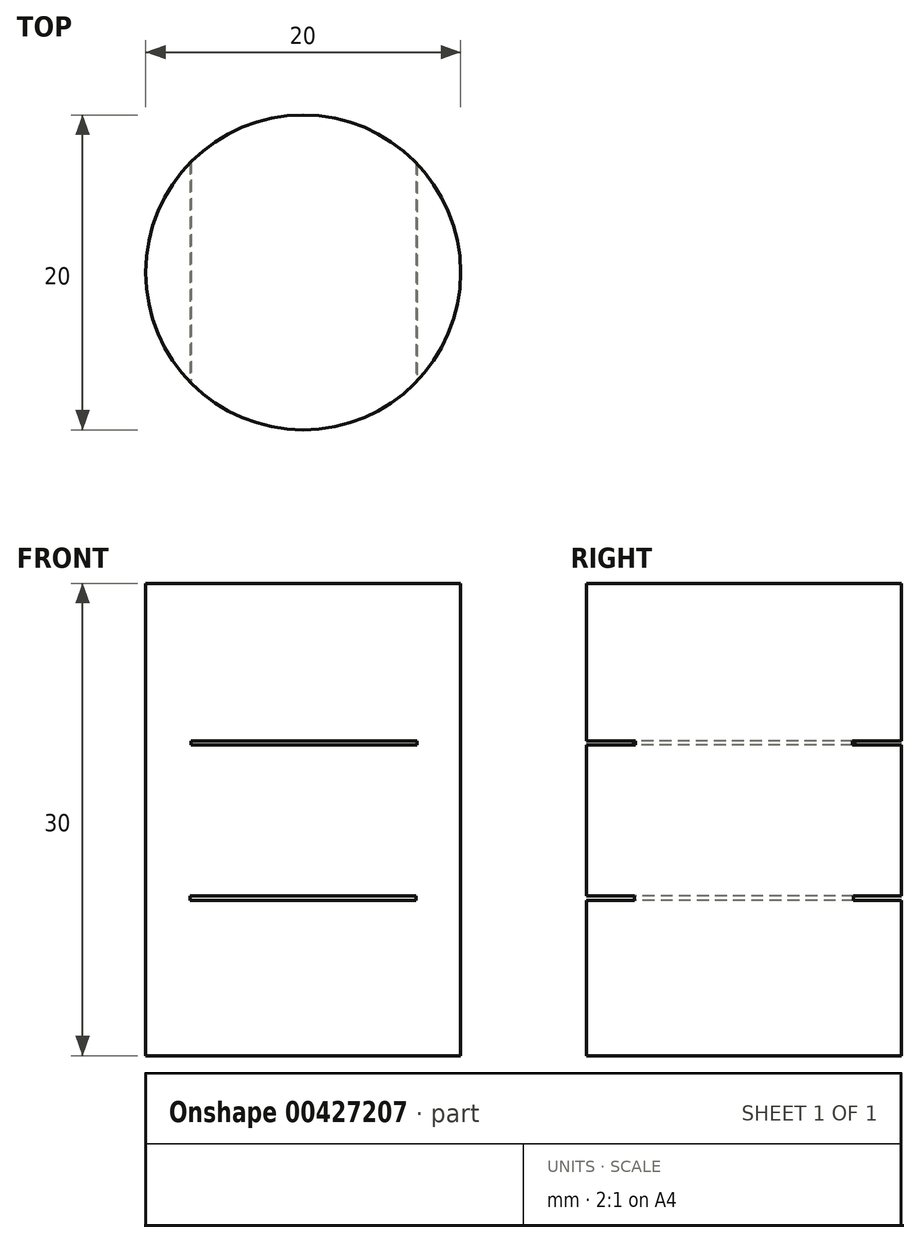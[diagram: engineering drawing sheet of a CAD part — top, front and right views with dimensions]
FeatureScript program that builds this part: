
annotation { "Feature Type Name" : "Feature", "Feature Type Description" : "" }
export const myFeature = defineFeature(function(context is Context, id is Id, definition is map)
    precondition{}
    {
        {
            var Q0;
            Q0=qCreatedBy(makeId("Top.planeOp"),FACE);
            var sketch = newSketch(context, id + "F0", { "sketchPlane" : qUnion([Q0])});
            skCircle(sketch, "E0", {"center": v(0, 0) * mm, "radius": 10 * mm});
            skSolve(sketch);
        }
        {
            var Q0;
            Q0=makeQuery(id+"F0.imprint","IMPRINT",FACE,{"disambiguationData":[TD([[makeQuery(id+"F0.imprint","IMPRINT",EDGE,{"derivedFrom":sQuery(id+"F0.wireOp",EDGE,"E0")}),1.0]])]});
            extrude(context, id + "F1", {"entities" : qUnion([Q0]), "depth" : 30 * mm});
        }
        {
            var Q0;
            Q0=qCreatedBy(makeId("Front.planeOp"),FACE);
            var sketch = newSketch(context, id + "F2", { "sketchPlane" : qUnion([Q0])});
            skLineSegment(sketch, "E1.bottom", {"start": v(-7.18, 9.87) * mm, "end": v(7.18, 9.87) * mm});
            skLineSegment(sketch, "E1.top", {"start": v(-7.18, 10.13) * mm, "end": v(7.18, 10.13) * mm});
            skLineSegment(sketch, "E1.left", {"start": v(-7.18, 9.87) * mm, "end": v(-7.18, 10.13) * mm});
            skLineSegment(sketch, "E1.right", {"start": v(7.18, 9.87) * mm, "end": v(7.18, 10.13) * mm});
            skPoint(sketch, "E1.middle", {"position": v(0, 10) * mm});
            skLineSegment(sketch, "E2.bottom", {"start": v(-7.1, 19.73) * mm, "end": v(7.25, 19.73) * mm});
            skLineSegment(sketch, "E2.top", {"start": v(-7.1, 20) * mm, "end": v(7.25, 20) * mm});
            skLineSegment(sketch, "E2.left", {"start": v(-7.1, 19.73) * mm, "end": v(-7.1, 20) * mm});
            skLineSegment(sketch, "E2.right", {"start": v(7.25, 19.73) * mm, "end": v(7.25, 20) * mm});
            skPoint(sketch, "E2.middle", {"position": v(0.07, 19.87) * mm});
            skSolve(sketch);
        }
        {
            var Q0;
            Q0 = qSketchRegion(id + "F2", true);
            extrude(context, id + "F3", {"entities" : qUnion([Q0]), "operationType" : NewBodyOperationType.REMOVE, "endBound" : BoundingType.SYMMETRIC, "oppositeDirection" : true, "depth" : 25.4 * mm});
        }
    });
